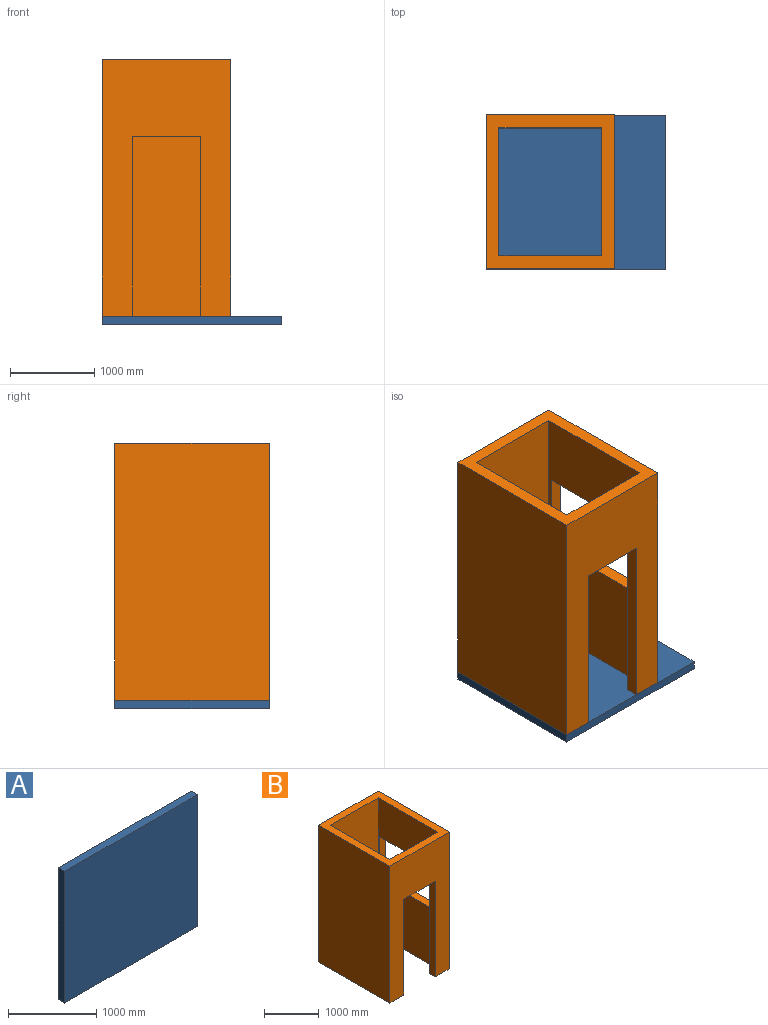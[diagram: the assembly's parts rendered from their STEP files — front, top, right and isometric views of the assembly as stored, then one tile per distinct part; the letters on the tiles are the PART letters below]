
ASSEMBLY  parts=2 mates=1
PART A: 6 faces, bbox 2133.6x101.6x1828.8 mm
  f0: plane 1828.8x101.6mm, normal (1,0,0), area 185806.1mm2, adj f1,f3,f4,f5
  f1: plane 2133.6x101.6mm, normal (0,0,1), area 216773.8mm2, adj f0,f2,f4,f5
  f2: plane 1828.8x101.6mm, normal (-1,0,0), area 185806.1mm2, adj f1,f3,f4,f5
  f3: plane 2133.6x101.6mm, normal (0,0,-1), area 216773.8mm2, adj f0,f2,f4,f5
  f4: plane 2133.6x1828.8mm, normal (0,-1,0), area 3901927.7mm2, adj f0,f1,f2,f3
  f5: plane 2133.6x1828.8mm, normal (0,1,0), area 3901927.7mm2, adj f0,f1,f2,f3
PART B: 17 faces, bbox 1524x1828.8x3048 mm
  f0: plane 3048x1828.8mm, normal (1,0,0), area 4235972.7mm2, adj f1,f3,f4,f5,f13,f14,f15,f16
  f1: plane 3048x1524mm, normal (0,1,0), area 4645152mm2, adj f0,f2,f4,f5
  f2: plane 3048x1828.8mm, normal (-1,0,0), area 5574182.4mm2, adj f1,f3,f4,f5
  f3: plane 3048x1524mm, normal (0,-1,0), area 2910961.9mm2, adj f0,f2,f4,f5,f10,f11,f12
  f4: plane 1828.8x1524mm, normal (0,0,1), area 929030.4mm2, adj f0,f1,f2,f3,f6,f7,f8,f9
  f5: plane 1828.8x1524mm, normal (0,0,-1), area 805159.7mm2, adj f0,f1,f2,f3,f6,f7,f8,f9
  f6: plane 3048x1524mm, normal (-1,0,0), area 3306942.3mm2, adj f4,f5,f7,f9,f13,f14,f15,f16
  f7: plane 3048x1219.2mm, normal (0,-1,0), area 3716121.6mm2, adj f4,f5,f6,f8
  f8: plane 3048x1524mm, normal (1,0,0), area 4645152mm2, adj f4,f5,f7,f9
  f9: plane 3048x1219.2mm, normal (0,1,0), area 1981931.5mm2, adj f4,f5,f6,f8,f10,f11,f12
  f10: plane 812.8x152.4mm, normal (0,0,-1), area 123870.7mm2, adj f3,f9,f11,f12
  f11: plane 2133.6x152.4mm, normal (1,0,0), area 325160.6mm2, adj f3,f5,f9,f10
  f12: plane 2133.6x152.4mm, normal (-1,0,0), area 325160.6mm2, adj f3,f5,f9,f10
  f13: plane 930.17x152.4mm, normal (0,-1,0), area 141758.4mm2, adj f0,f6,f14,f16
  f14: plane 1438.67x152.4mm, normal (0,0,-1), area 219253mm2, adj f0,f6,f13,f15
  f15: plane 930.17x152.4mm, normal (0,1,0), area 141758.4mm2, adj f0,f6,f14,f16
  f16: plane 1438.67x152.4mm, normal (0,0,1), area 219253mm2, adj f0,f6,f13,f15
PLACE A rot(axis=(-1,0,0),90deg) t=(-2203.95,-1420.38,-59.52)mm
PLACE B t=(-2508.75,-1420.38,42.08)mm
MATE fastened A.f4 <-> B.f5  axis (0,0,1) through (-3270.75,-505.98,42.08)mm
